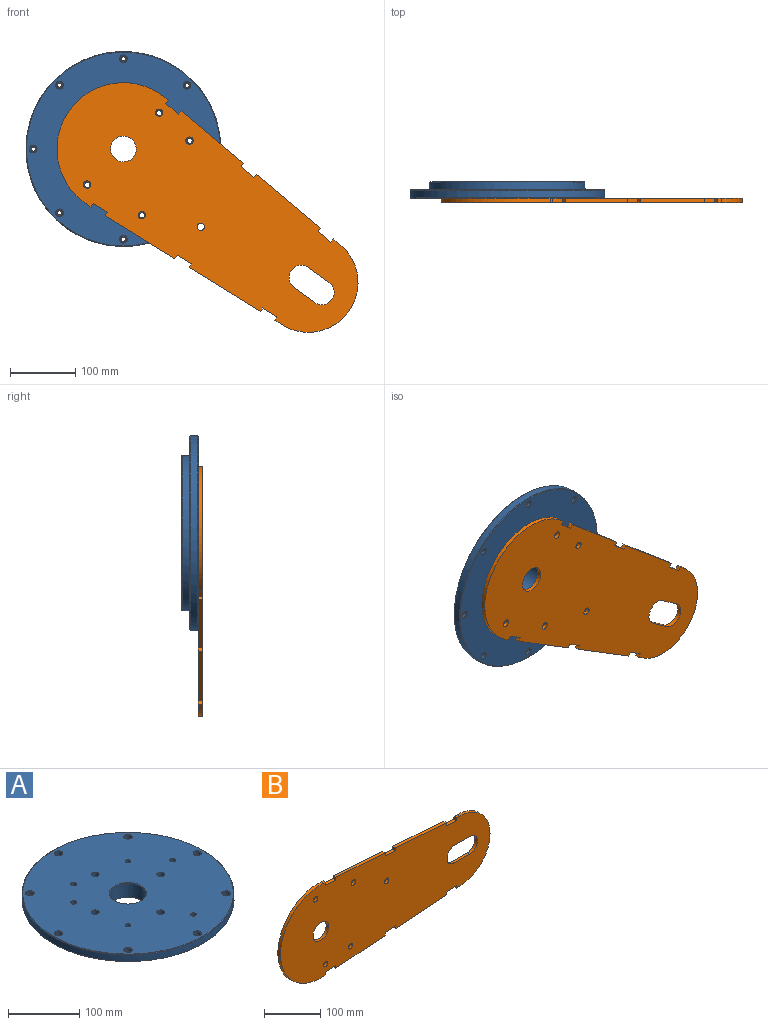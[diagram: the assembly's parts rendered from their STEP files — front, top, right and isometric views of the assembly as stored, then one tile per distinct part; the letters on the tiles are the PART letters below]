
ASSEMBLY  parts=2 mates=1
PART A: 64 faces, bbox 298.5x298.5x25.4 mm
  f0: plane 296.82x296.82mm, normal (0,0,1), area 65495.5mm2, adj f32,f33,f34,f35,f36,f37,f38,f39
  f1: cylinder r=25.4mm len=50.8mm, axis (0,0,-1), area 3794.2mm2, adj f41,f42
  f2: plane 236.4x236.4mm, normal (0,0,-1), area 41062.1mm2, adj f42,f43,f54,f55,f56,f57,f58,f59
  f3: cylinder r=119.01mm len=238.02mm, axis (0,0,-1), area 12402.7mm2, adj f4,f43
  f4: plane 258.09x258.09mm, normal (0,0,-1), area 7818.6mm2, adj f3,f5
  f5: cylinder r=129.04mm len=258.09mm, axis (0,0,-1), area 3253.9mm2, adj f4,f52
  f6: plane 296.82x296.82mm, normal (0,0,-1), area 15803mm2, adj f44,f45,f46,f47,f48,f49,f50,f51
  f7: cylinder r=149.22mm len=298.45mm, axis (0,0,-1), area 10502.5mm2, adj f40,f53
  f8: cylinder r=3.26mm len=6.53mm, axis (0,0,1), area 116.2mm2, adj f9,f50
  f9: plane 10.16x10.16mm, normal (0,0,1), area 47.6mm2, adj f8,f10
  f10: cylinder r=5.08mm len=10.16mm, axis (0,0,1), area 176.7mm2, adj f9,f38
  f11: cylinder r=3.26mm len=6.53mm, axis (0,0,1), area 116.2mm2, adj f12,f49
  f12: plane 10.16x10.16mm, normal (0,0,1), area 47.6mm2, adj f11,f13
  f13: cylinder r=5.08mm len=10.16mm, axis (0,0,1), area 176.7mm2, adj f12,f37
  f14: cylinder r=3.26mm len=6.53mm, axis (0,0,1), area 116.2mm2, adj f15,f48
  f15: plane 10.16x10.16mm, normal (0,0,1), area 47.6mm2, adj f14,f16
  f16: cylinder r=5.08mm len=10.16mm, axis (0,0,1), area 176.7mm2, adj f15,f36
  f17: cylinder r=3.26mm len=6.53mm, axis (0,0,1), area 116.2mm2, adj f18,f47
  f18: plane 10.16x10.16mm, normal (0,0,1), area 47.6mm2, adj f17,f19
  f19: cylinder r=5.08mm len=10.16mm, axis (0,0,1), area 176.7mm2, adj f18,f35
  f20: cylinder r=3.26mm len=6.53mm, axis (0,0,1), area 116.2mm2, adj f21,f46
  f21: plane 10.16x10.16mm, normal (0,0,1), area 47.6mm2, adj f20,f22
  f22: cylinder r=5.08mm len=10.16mm, axis (0,0,1), area 176.7mm2, adj f21,f34
  f23: cylinder r=3.26mm len=6.53mm, axis (0,0,1), area 116.2mm2, adj f24,f45
  f24: plane 10.16x10.16mm, normal (0,0,1), area 47.6mm2, adj f23,f25
  f25: cylinder r=5.08mm len=10.16mm, axis (0,0,1), area 176.7mm2, adj f24,f33
  f26: cylinder r=3.26mm len=6.53mm, axis (0,0,1), area 116.2mm2, adj f27,f44
  f27: plane 10.16x10.16mm, normal (0,0,1), area 47.6mm2, adj f26,f28
  f28: cylinder r=5.08mm len=10.16mm, axis (0,0,1), area 176.7mm2, adj f27,f32
  f29: cylinder r=3.26mm len=6.53mm, axis (0,0,1), area 116.2mm2, adj f30,f51
  f30: plane 10.16x10.16mm, normal (0,0,1), area 47.6mm2, adj f29,f31
  f31: cylinder r=5.08mm len=10.16mm, axis (0,0,1), area 176.7mm2, adj f30,f39
  f32: cone r=5.08mm half-angle=45deg, axis (0,0,1), area 39.6mm2, adj f0,f28
  f33: cone r=5.08mm half-angle=45deg, axis (0,0,1), area 39.6mm2, adj f0,f25
  f34: cone r=5.08mm half-angle=45deg, axis (0,0,1), area 39.6mm2, adj f0,f22
  f35: cone r=5.08mm half-angle=45deg, axis (0,0,1), area 39.6mm2, adj f0,f19
  f36: cone r=5.08mm half-angle=45deg, axis (0,0,1), area 39.6mm2, adj f0,f16
  f37: cone r=5.08mm half-angle=45deg, axis (0,0,1), area 39.6mm2, adj f0,f13
  f38: cone r=5.08mm half-angle=45deg, axis (0,0,1), area 39.6mm2, adj f0,f10
  f39: cone r=5.08mm half-angle=45deg, axis (0,0,1), area 39.6mm2, adj f0,f31
  f40: cone r=149.22mm half-angle=45deg, axis (0,0,-1), area 1074.8mm2, adj f0,f7
  f41: cone r=26.21mm half-angle=45deg, axis (0,0,1), area 186.4mm2, adj f0,f1
  f42: cone r=25.4mm half-angle=45deg, axis (0,0,-1), area 186.4mm2, adj f1,f2
  f43: cone r=118.2mm half-angle=45deg, axis (0,0,1), area 856.6mm2, adj f2,f3
  f44: cone r=3.26mm half-angle=45deg, axis (0,0,-1), area 26.5mm2, adj f6,f26
  f45: cone r=3.26mm half-angle=45deg, axis (0,0,-1), area 26.5mm2, adj f6,f23
  f46: cone r=3.26mm half-angle=45deg, axis (0,0,-1), area 26.5mm2, adj f6,f20
  f47: cone r=3.26mm half-angle=45deg, axis (0,0,-1), area 26.5mm2, adj f6,f17
  f48: cone r=3.26mm half-angle=45deg, axis (0,0,-1), area 26.5mm2, adj f6,f14
  f49: cone r=3.26mm half-angle=45deg, axis (0,0,-1), area 26.5mm2, adj f6,f11
  f50: cone r=3.26mm half-angle=45deg, axis (0,0,-1), area 26.5mm2, adj f6,f8
  f51: cone r=3.26mm half-angle=45deg, axis (0,0,-1), area 26.5mm2, adj f6,f29
  f52: cone r=129.04mm half-angle=45deg, axis (0,0,-1), area 934.9mm2, adj f5,f6
  f53: cone r=148.41mm half-angle=45deg, axis (0,0,1), area 1074.8mm2, adj f6,f7
  f54: cylinder r=5.36mm len=25.4mm, axis (0,0,1), area 855.1mm2, adj f0,f2
  f55: cylinder r=5.36mm len=25.4mm, axis (0,0,1), area 855.1mm2, adj f0,f2
  f56: cylinder r=5.36mm len=25.4mm, axis (0,0,1), area 855.1mm2, adj f0,f2
  f57: cylinder r=5.36mm len=25.4mm, axis (0,0,1), area 855.1mm2, adj f0,f2
  f58: cylinder r=3.97mm len=25.4mm, axis (0,0,1), area 633.4mm2, adj f0,f2
  f59: cylinder r=3.97mm len=25.4mm, axis (0,0,1), area 633.4mm2, adj f0,f2
  f60: cylinder r=3.97mm len=25.4mm, axis (0,0,1), area 633.4mm2, adj f0,f2
  f61: cylinder r=3.97mm len=25.4mm, axis (0,0,1), area 633.4mm2, adj f0,f2
  f62: cylinder r=4.22mm len=25.4mm, axis (0,0,1), area 672.9mm2, adj f0,f2
  f63: cylinder r=4.22mm len=25.4mm, axis (0,0,1), area 672.9mm2, adj f0,f2
PART B: 40 faces, bbox 527.1x6.4x203.2 mm
  f0: plane 6.35x4.58mm, normal (0.07,0,-1), area 29.1mm2, adj f7,f8,f15,f27
  f1: plane 128.32x9.43mm, normal (0.07,0,-1), area 817mm2, adj f7,f8,f21,f24
  f2: plane 125x9.19mm, normal (0.07,0,-1), area 795.9mm2, adj f7,f8,f25,f28
  f3: plane 7.91x6.35mm, normal (0.07,0,1), area 50.4mm2, adj f7,f8,f13,f34
  f4: plane 125x9.19mm, normal (0.07,0,1), area 795.9mm2, adj f7,f8,f19,f31
  f5: plane 128.32x9.43mm, normal (0.07,0,1), area 817mm2, adj f7,f8,f18,f33
  f6: plane 6.35x4.58mm, normal (0.07,0,1), area 29.1mm2, adj f7,f8,f15,f30
  f7: plane 527.05x203.2mm, normal (0,-1,0), area 82264.7mm2, adj f0,f1,f2,f3,f4,f5,f6,f9
  f8: plane 527.05x203.2mm, normal (0,1,0), area 82264.7mm2, adj f0,f1,f2,f3,f4,f5,f6,f9
  f9: cylinder r=19.05mm len=38.1mm, axis (0,1,0), area 380mm2, adj f7,f8,f10,f16
  f10: plane 38.1x6.35mm, normal (0,0,-1), area 241.9mm2, adj f7,f8,f9,f11
  f11: cylinder r=19.05mm len=38.1mm, axis (0,1,0), area 380mm2, adj f7,f8,f10,f16
  f12: plane 7.91x6.35mm, normal (0.07,0,-1), area 50.4mm2, adj f7,f8,f13,f22
  f13: cylinder r=76.2mm len=152.4mm, axis (0,1,0), area 1520.1mm2, adj f3,f7,f8,f12
  f14: cylinder r=19.69mm len=39.37mm, axis (0,1,0), area 785.4mm2, adj f7,f8
  f15: cylinder r=101.6mm len=203.2mm, axis (0,1,0), area 2121.5mm2, adj f0,f6,f7,f8
  f16: plane 38.1x6.35mm, normal (0,0,1), area 241.9mm2, adj f7,f8,f9,f11
  f17: plane 25.33x6.35mm, normal (0.07,0,1), area 161.3mm2, adj f7,f8,f18,f19
  f18: plane 6.35x6.33mm, normal (-1,0,0.07), area 40.3mm2, adj f5,f7,f8,f17
  f19: plane 6.35x6.33mm, normal (1,0,-0.07), area 40.3mm2, adj f4,f7,f8,f17
  f20: plane 25.33x6.35mm, normal (0.07,0,-1), area 161.3mm2, adj f7,f8,f21,f22
  f21: plane 6.35x6.33mm, normal (1,0,0.07), area 40.3mm2, adj f1,f7,f8,f20
  f22: plane 6.35x6.33mm, normal (-1,0,-0.07), area 40.3mm2, adj f7,f8,f12,f20
  f23: plane 25.33x6.35mm, normal (0.07,0,-1), area 161.3mm2, adj f7,f8,f24,f25
  f24: plane 6.35x6.33mm, normal (-1,0,-0.07), area 40.3mm2, adj f1,f7,f8,f23
  f25: plane 6.35x6.33mm, normal (1,0,0.07), area 40.3mm2, adj f2,f7,f8,f23
  f26: plane 25.33x6.35mm, normal (0.07,0,-1), area 161.3mm2, adj f7,f8,f27,f28
  f27: plane 6.35x6.33mm, normal (1,0,0.07), area 40.3mm2, adj f0,f7,f8,f26
  f28: plane 6.35x6.33mm, normal (-1,0,-0.07), area 40.3mm2, adj f2,f7,f8,f26
  f29: plane 25.33x6.35mm, normal (0.07,0,1), area 161.3mm2, adj f7,f8,f30,f31
  f30: plane 6.35x6.33mm, normal (1,0,-0.07), area 40.3mm2, adj f6,f7,f8,f29
  f31: plane 6.35x6.33mm, normal (-1,0,0.07), area 40.3mm2, adj f4,f7,f8,f29
  f32: plane 25.33x6.35mm, normal (0.07,0,1), area 161.3mm2, adj f7,f8,f33,f34
  f33: plane 6.35x6.33mm, normal (1,0,-0.07), area 40.3mm2, adj f5,f7,f8,f32
  f34: plane 6.35x6.33mm, normal (-1,0,0.07), area 40.3mm2, adj f3,f7,f8,f32
  f35: cylinder r=5.56mm len=11.11mm, axis (0,-1,0), area 221.7mm2, adj f7,f8
  f36: cylinder r=5.56mm len=11.11mm, axis (0,-1,0), area 221.7mm2, adj f7,f8
  f37: cylinder r=5.56mm len=11.11mm, axis (0,-1,0), area 221.7mm2, adj f7,f8
  f38: cylinder r=5.56mm len=11.11mm, axis (0,-1,0), area 221.7mm2, adj f7,f8
  f39: cylinder r=5.56mm len=11.11mm, axis (0,-1,0), area 221.7mm2, adj f7,f8
PLACE A rot(axis=(1,0,0),90deg) t=(17.88,58.63,32.41)mm fixed
PLACE B rot(axis=(-0.95,0,0.31),180deg) t=(301.01,52.28,-172.08)mm
MATE revolute B.f14 <-> A.f1  axis (0,1,0) through (17.88,58.63,32.41)mm
